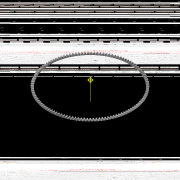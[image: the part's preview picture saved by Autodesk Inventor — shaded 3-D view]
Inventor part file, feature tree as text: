
AUTODESK INVENTOR PART (.ipt)
format: ipt  version: 2017 (Build 210142000, 142)  size: 1,804,288 bytes
history: native  units: mm
features: other x24, loft x2, pattern_circular x2, sketch x2, extrude x1
ambient origin geometry x6: Origin, XZ Plane, X Axis, Y Axis, Z Axis, Center Point
bodies: Solid1 (feature_tree)
feature tree (31):
  other  "Top Point"
  other  "Mesh Plane2"
  other  "Teeth Body"
  other  "Start Point"
  other  "Tooth Plane"
  other  "Start Sketch"
  other  "End Point"
  other  "3D Sketch Right"
  other  "End Plane Right"
  loft  "Loft Right"
  pattern_circular  "Circular Pattern Right"  [2 undecoded]
  other  "3D Sketch Left"
  other  "End Plane Left"
  loft  "Loft Left"
  pattern_circular  "Circular Pattern Left"  Angle=90.0deg  [1 undecoded]
  other  "Fix Body"
  extrude  "Extrusion1"  Depth=10.0mm
  other  "Mesh Plane"
  other  "Top Plane"
  other  "Teeth Body Sketch"
  other  "End Plane"
  other  "End Sketch"
  other  "Helical Curve Left"
  other  "End Sketch Left"
  other  "Body Sketch"
  sketch  "Sketch6"  dims[d0=302.26mm d1=301.497629mm]
  other  "Srf1"
  other  "Helical Curve Right"
  other  "End Sketch Right"
  sketch  "Sketch8"  dims[d2=302.895309mm d3=7.62mm d4=16.529941mm d5=90.0deg d7=414.205299mm d8=393.316689mm d9=1072.681211mm d11=7.8994mm d12=393.139419mm d15=373.313174mm d16=1018.126202mm d17=0.0mm d18=90.0deg d19=0.0mm d20=90.0deg d21=1190.0mm d22=360.0deg d26=314.208686mm d27=0.987905mm d28=302.26mm d29=-14.454072mm d30=393.139419mm d31=373.313174mm d32=1018.126202mm d35=0.0mm d37=0.0mm d39=0.0mm d40=90.0deg d41=1190.0mm d42=360.0deg d46=90.0deg d47=90.0deg d48=0.0mm d49=0.0mm d50=90.0deg d51=0.263999mm d52=0.0mm d53=0.0mm d54=0.0mm d56=18.022547mm d57=1212.66853mm d58=1204.73357mm d59=1150.993968mm d60=1143.462569mm d61=1150.993968mm d62=1143.462569mm d63=90.0deg d64=90.0deg d65=314.208686mm d66=31.5mm d67=302.26mm d68=-14.454072mm d69=0.987905mm d70=373.313174mm d71=1018.126202mm d72=393.139419mm d73=1143.462569mm d74=1150.993968mm d75=0.0mm d76=90.0deg d77=0.0mm d78=90.0deg d79=0.0mm d80=90.0deg d81=1190.0mm d82=360.0deg d84=10.0mm d85=20.0mm d86=20.0mm d87=10.0mm d88=0.0mm d89=0.0mm d90=25.4mm d91=0.0mm d92=286.4104mm]
  other  "Pitch Diameter"
note: 3 required parameter values undecoded (feature->parameter linkage not recoverable at this tier; creation-order binding heuristic only, values carry confidence <= 0.55)
